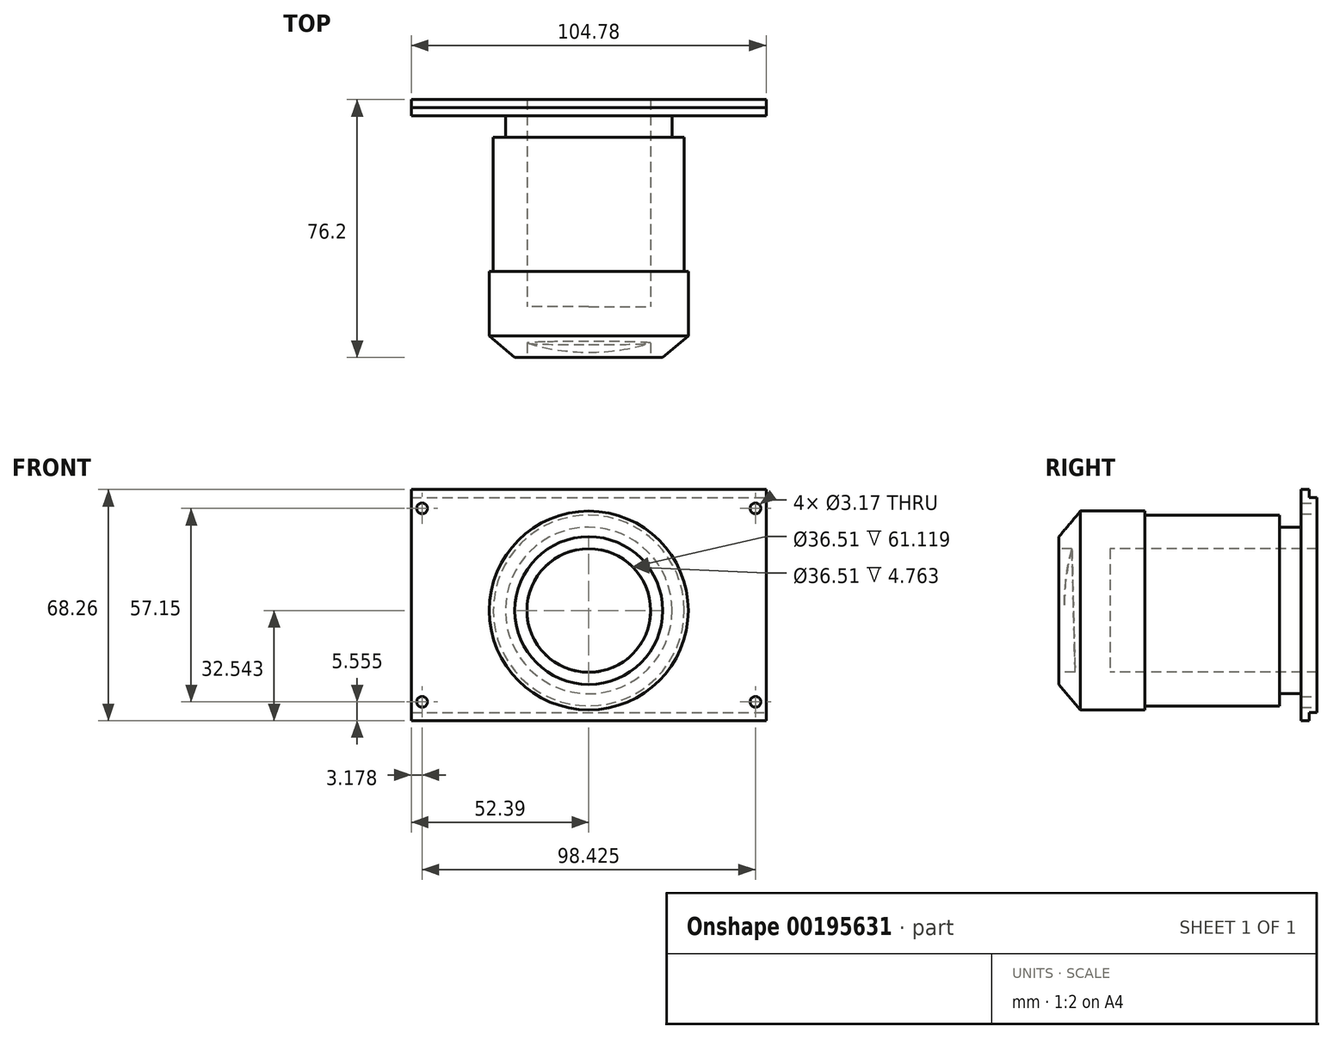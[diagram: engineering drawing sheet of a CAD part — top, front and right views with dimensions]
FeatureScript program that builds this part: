
annotation { "Feature Type Name" : "Feature", "Feature Type Description" : "" }
export const myFeature = defineFeature(function(context is Context, id is Id, definition is map)
    precondition{}
    {
        {
            var Q0;
            Q0=qCreatedBy(makeId("Front.planeOp"),FACE);
            var sketch = newSketch(context, id + "F0", { "sketchPlane" : qUnion([Q0])});
            skLineSegment(sketch, "E0.bottom", {"start": v(-52.39, 34.13) * mm, "end": v(52.39, 34.13) * mm});
            skLineSegment(sketch, "E0.top", {"start": v(-52.39, -34.13) * mm, "end": v(52.39, -34.13) * mm});
            skLineSegment(sketch, "E0.left", {"start": v(-52.39, 34.13) * mm, "end": v(-52.39, -34.13) * mm});
            skLineSegment(sketch, "E0.right", {"start": v(52.39, 34.13) * mm, "end": v(52.39, -34.13) * mm});
            skSolve(sketch);
        }
        {
            var Q0;
            Q0 = qSketchRegion(id + "F0", true);
            extrude(context, id + "F1", {"entities" : qUnion([Q0]), "depth" : 4.76 * mm});
        }
        {
            var Q0;
            Q0=makeQuery(id+"F1.opExtrude","SWEPT_FACE",FACE,{"disambiguationData":[OSD([sQuery(id+"F0.wireOp",EDGE,"E0.right")])]});
            var sketch = newSketch(context, id + "F2", { "sketchPlane" : qUnion([Q0])});
            skLineSegment(sketch, "E1.bottom", {"start": v(-2.38, 34.13) * mm, "end": v(0, 34.13) * mm});
            skLineSegment(sketch, "E1.top", {"start": v(-2.38, 31.75) * mm, "end": v(0, 31.75) * mm});
            skLineSegment(sketch, "E1.left", {"start": v(-2.38, 34.13) * mm, "end": v(-2.38, 31.75) * mm});
            skLineSegment(sketch, "E1.right", {"start": v(0, 34.13) * mm, "end": v(0, 31.75) * mm});
            skLineSegment(sketch, "E2.MirrorCS", {"start": v(0, -34.13) * mm, "end": v(0, -31.75) * mm});
            skLineSegment(sketch, "E3.MirrorCS", {"start": v(-2.38, -34.13) * mm, "end": v(-2.38, -31.75) * mm});
            skLineSegment(sketch, "E4.MirrorCS", {"start": v(-2.38, -34.13) * mm, "end": v(0, -34.13) * mm});
            skLineSegment(sketch, "E5.MirrorCS", {"start": v(-2.38, -31.75) * mm, "end": v(0, -31.75) * mm});
            skSolve(sketch);
        }
        {
            var Q0;
            Q0 = qSketchRegion(id + "F2", true);
            extrude(context, id + "F3", {"entities" : qUnion([Q0]), "operationType" : NewBodyOperationType.REMOVE, "endBound" : BoundingType.UP_TO_NEXT, "oppositeDirection" : true, "depth" : 25.4 * mm});
        }
        {
            var Q0;
            Q0=makeQuery(id+"F1.opExtrude","CAP_FACE",FACE,{"disambiguationData":[OSD([sQuery(id+"F0.wireOp",EDGE,"E0.bottom"),sQuery(id+"F0.wireOp",EDGE,"E0.top"),sQuery(id+"F0.wireOp",EDGE,"E0.left"),sQuery(id+"F0.wireOp",EDGE,"E0.right")])],"isStart":true});
            var sketch = newSketch(context, id + "F4", { "sketchPlane" : qUnion([Q0])});
            skCircle(sketch, "E6", {"center": v(-49.21, 28.57) * mm, "radius": 1.59 * mm});
            skCircle(sketch, "E7.MirrorC", {"center": v(49.21, 28.57) * mm, "radius": 1.59 * mm});
            skCircle(sketch, "E8.MirrorC", {"center": v(-49.21, -28.57) * mm, "radius": 1.59 * mm});
            skCircle(sketch, "E9.MirrorC", {"center": v(49.21, -28.57) * mm, "radius": 1.59 * mm});
            skSolve(sketch);
        }
        {
            var Q0;
            Q0 = qSketchRegion(id + "F4", true);
            extrude(context, id + "F5", {"entities" : qUnion([Q0]), "operationType" : NewBodyOperationType.REMOVE, "endBound" : BoundingType.UP_TO_NEXT, "oppositeDirection" : true, "depth" : 4.76 * mm});
        }
        {
            var Q0;
            Q0=qCreatedBy(makeId("Right.planeOp"),FACE);
            var sketch = newSketch(context, id + "F6", { "sketchPlane" : qUnion([Q0])});
            skLineSegment(sketch, "E10", {"start": v(-4.76, -26.2) * mm, "end": v(-11.11, -26.2) * mm});
            skLineSegment(sketch, "E11", {"start": v(-11.11, -26.2) * mm, "end": v(-11.11, -29.77) * mm});
            skLineSegment(sketch, "E12", {"start": v(-11.11, -29.77) * mm, "end": v(-50.8, -29.77) * mm});
            skLineSegment(sketch, "E13", {"start": v(-50.8, -29.77) * mm, "end": v(-50.8, -30.96) * mm});
            skLineSegment(sketch, "E14", {"start": v(-50.8, -30.96) * mm, "end": v(-69.85, -30.96) * mm});
            skLineSegment(sketch, "E15", {"start": v(-69.85, -30.96) * mm, "end": v(-76.2, -23.42) * mm});
            skLineSegment(sketch, "E16", {"start": v(-76.2, -23.42) * mm, "end": v(-76.2, -1.59) * mm});
            skLineSegment(sketch, "E17", {"start": v(-4.76, -1.59) * mm, "end": v(-87.25, -1.59) * mm});
            skLineSegment(sketch, "E18", {"start": v(-4.76, -1.59) * mm, "end": v(-4.76, -26.2) * mm});
            skSolve(sketch);
        }
        {
            var Q0;
            Q0 = qSketchRegion(id + "F6", true);
            var Q1;
            Q1=sQuery(id+"F6.wireOp",EDGE,"E17");
            revolve(context, id + "F7", {"operationType" : NewBodyOperationType.ADD, "entities" : qUnion([Q0]), "axis" : qUnion([Q1]), "revolveType" : RevolveType.FULL});
        }
        {
            var Q0;
            Q0=makeQuery(id+"F7.opRevolve","SWEPT_FACE",FACE,{"disambiguationData":[OSD([sQuery(id+"F6.wireOp",EDGE,"E16")])]});
            var sketch = newSketch(context, id + "F8", { "sketchPlane" : qUnion([Q0])});
            skCircle(sketch, "E19", {"center": v(0, -1.59) * mm, "radius": 18.26 * mm});
            skSolve(sketch);
        }
        {
            var Q0;
            Q0 = qSketchRegion(id + "F8", true);
            var Q1;
            Q1=makeQuery(id+"F1.opExtrude","CAP_FACE",FACE,{"disambiguationData":[OSD([sQuery(id+"F0.wireOp",EDGE,"E0.bottom"),sQuery(id+"F0.wireOp",EDGE,"E0.top"),sQuery(id+"F0.wireOp",EDGE,"E0.left"),sQuery(id+"F0.wireOp",EDGE,"E0.right")])],"isStart":true});
            extrude(context, id + "F9", {"entities" : qUnion([Q0]), "operationType" : NewBodyOperationType.REMOVE, "endBound" : BoundingType.UP_TO_SURFACE, "oppositeDirection" : true, "endBoundEntityFace" : qUnion([Q1]), "depth" : 25.4 * mm});
        }
        {
            var Q0;
            Q0=qCreatedBy(makeId("Right.planeOp"),FACE);
            var sketch = newSketch(context, id + "F10", { "sketchPlane" : qUnion([Q0])});
            skLineSegment(sketch, "E20", {"start": v(-61.12, 0) * mm, "end": v(-61.12, 19.84) * mm});
            skLineSegment(sketch, "E21", {"start": v(-61.12, 19.84) * mm, "end": v(-71.44, 19.84) * mm});
            skPoint(sketch, "E22", {"position": v(-74.61, 0) * mm});
            skArc(sketch, "E23", {"start": v(-71.44, 19.84) * mm, "mid": v(-73.81, 10.05) * mm, "end": v(-74.61, 0) * mm});
            skLineSegment(sketch, "E24.trimOffspring", {"start": v(-61.12, 0) * mm, "end": v(-74.61, 0) * mm});
            skSolve(sketch);
        }
        {
            var Q0;
            Q0 = qSketchRegion(id + "F10", true);
            var Q1;
            Q1=sQuery(id+"F10.wireOp",EDGE,"E21");
            var Q2;
            Q2=sQuery(id+"F10.wireOp",EDGE,"E23");
            var Q3;
            Q3=sQuery(id+"F10.wireOp",EDGE,"E20");
            var Q4;
            Q4=sQuery(id+"F10.wireOp",EDGE,"E24.trimOffspring");
            revolve(context, id + "F11", {"operationType" : NewBodyOperationType.ADD, "entities" : qUnion([Q0]), "surfaceEntities" : qUnion([Q1, Q2, Q3]), "axis" : qUnion([Q4]), "revolveType" : RevolveType.FULL});
        }
    });
